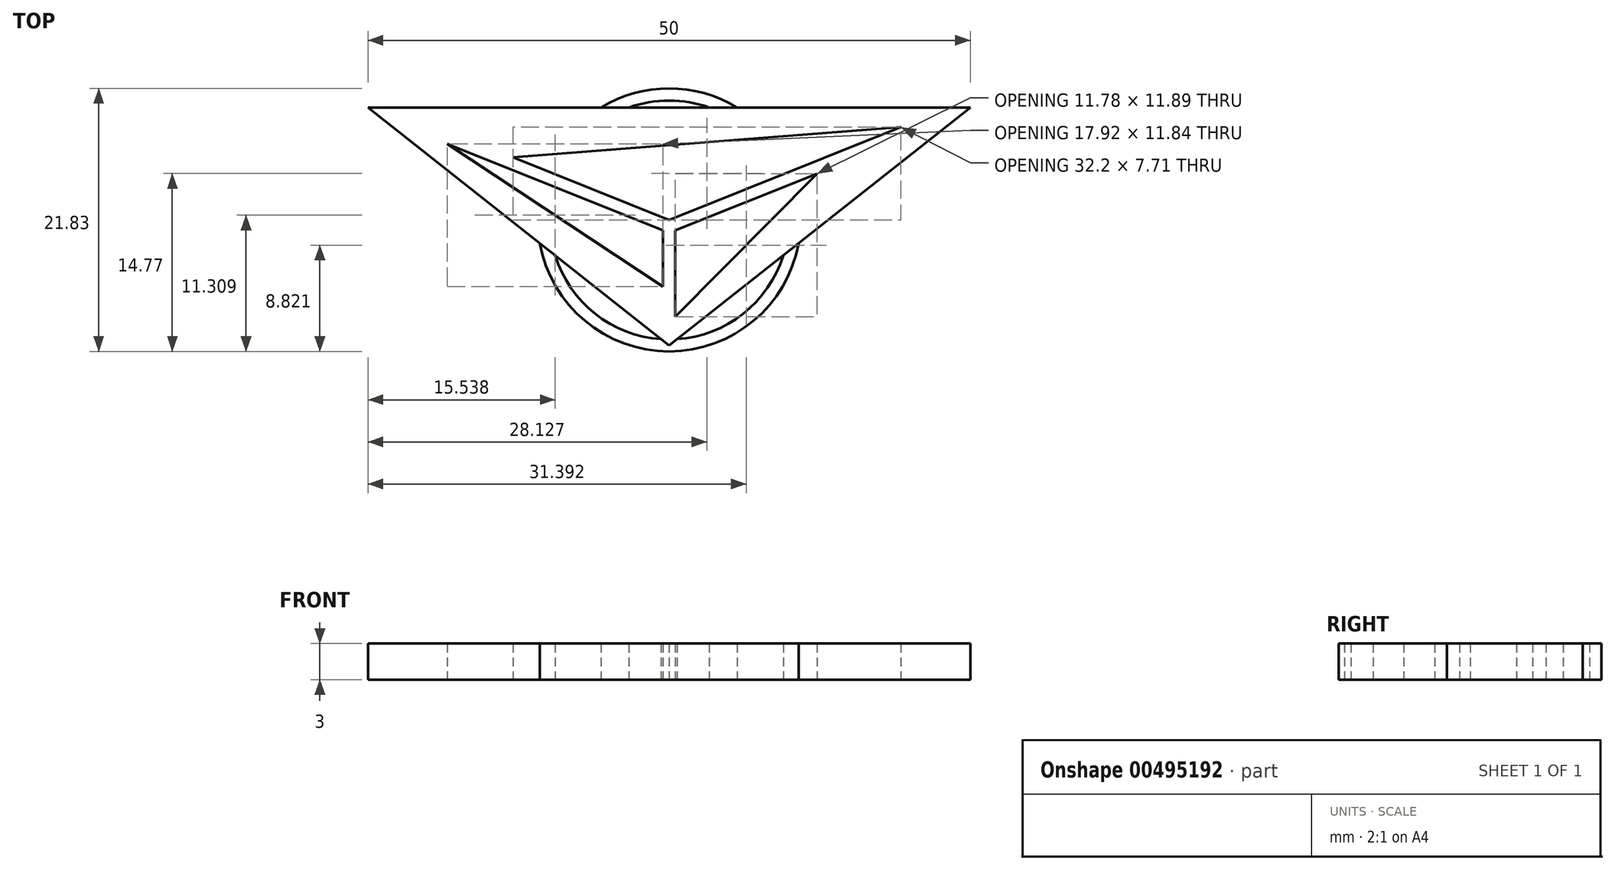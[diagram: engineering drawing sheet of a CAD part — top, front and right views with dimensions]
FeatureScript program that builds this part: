
annotation { "Feature Type Name" : "Feature", "Feature Type Description" : "" }
export const myFeature = defineFeature(function(context is Context, id is Id, definition is map)
    precondition{}
    {
        {
            var Q0;
            Q0=qCreatedBy(makeId("Top.planeOp"),FACE);
            var sketch = newSketch(context, id + "F0", { "sketchPlane" : qUnion([Q0])});
            skLineSegment(sketch, "E0", {"start": v(0, 0) * mm, "end": v(25, 0) * mm});
            skLineSegment(sketch, "E1", {"start": v(25, 0) * mm, "end": v(0, -19.75) * mm});
            skLineSegment(sketch, "E2", {"start": v(0, -19.75) * mm, "end": v(-25, 0) * mm});
            skLineSegment(sketch, "E3", {"start": v(-25, 0) * mm, "end": v(0, 0) * mm});
            skLineSegment(sketch, "E4.0", {"start": v(-22.12, -1) * mm, "end": v(0, -1) * mm});
            skPoint(sketch, "E5", {"position": v(0, -9.88) * mm});
            skLineSegment(sketch, "E6", {"start": v(0, -1) * mm, "end": v(22.12, -1) * mm});
            skLineSegment(sketch, "E7.0", {"start": v(22.12, -1) * mm, "end": v(0, -18.48) * mm});
            skLineSegment(sketch, "E8.0", {"start": v(0, -18.48) * mm, "end": v(-22.12, -1) * mm});
            skLineSegment(sketch, "E9", {"start": v(0, 0) * mm, "end": v(0, -19.75) * mm, "construction": true});
            skLineSegment(sketch, "E10", {"start": v(-22.12, -1) * mm, "end": v(0, -9.88) * mm, "construction": true});
            skLineSegment(sketch, "E11.0", {"start": v(-20.74, -2.1) * mm, "end": v(-0.5, -10.21) * mm});
            skLineSegment(sketch, "E12.0", {"start": v(-20.78, -1) * mm, "end": v(0, -9.34) * mm});
            skLineSegment(sketch, "E13.0", {"start": v(-0.5, -2.16) * mm, "end": v(-0.5, -18.08) * mm});
            skLineSegment(sketch, "E14.0", {"start": v(0.5, -2.08) * mm, "end": v(0.5, -18.08) * mm});
            skLineSegment(sketch, "E15", {"start": v(22.12, -1) * mm, "end": v(0, -9.88) * mm, "construction": true});
            skLineSegment(sketch, "E16.0", {"start": v(20.78, -1) * mm, "end": v(0, -9.34) * mm});
            skLineSegment(sketch, "E17.0", {"start": v(20.74, -2.1) * mm, "end": v(0.5, -10.21) * mm});
            skPoint(sketch, "E18", {"position": v(-14.02, -3.71) * mm});
            skPoint(sketch, "E19", {"position": v(13.45, -5.02) * mm});
            skPoint(sketch, "E20", {"position": v(-0.5, -15.46) * mm});
            skLineSegment(sketch, "E21", {"start": v(-14.02, -3.71) * mm, "end": v(20.78, -1) * mm, "construction": true});
            skLineSegment(sketch, "E22", {"start": v(13.45, -5.02) * mm, "end": v(0.5, -18.08) * mm, "construction": true});
            skLineSegment(sketch, "E23", {"start": v(-0.5, -15.46) * mm, "end": v(-20.74, -2.1) * mm, "construction": true});
            skLineSegment(sketch, "E24.0", {"start": v(-12.97, -4.13) * mm, "end": v(19.23, -1.62) * mm});
            skLineSegment(sketch, "E25.0", {"start": v(-15.07, -3.3) * mm, "end": v(14.34, -1) * mm});
            skLineSegment(sketch, "E26.0", {"start": v(12.28, -5.49) * mm, "end": v(0.5, -17.37) * mm});
            skLineSegment(sketch, "E27.0", {"start": v(14.62, -4.55) * mm, "end": v(3.75, -15.52) * mm});
            skLineSegment(sketch, "E28.0", {"start": v(-0.5, -14.86) * mm, "end": v(-18.42, -3.02) * mm});
            skLineSegment(sketch, "E29.0", {"start": v(-0.5, -16.06) * mm, "end": v(-16.11, -5.75) * mm});
            skPoint(sketch, "E30.positionSnap0", {"position": v(10.62, -6.15) * mm});
            skPoint(sketch, "E31", {"position": v(11.06, -5.44) * mm});
            skPoint(sketch, "E32", {"position": v(-9.47, -12.27) * mm});
            skPoint(sketch, "E33", {"position": v(-10.74, -11.26) * mm});
            skPoint(sketch, "E34", {"position": v(9.47, -12.27) * mm});
            skPoint(sketch, "E35", {"position": v(10.74, -11.26) * mm});
            skPoint(sketch, "E36", {"position": v(5.65, 0) * mm});
            skPoint(sketch, "E37", {"position": v(3.33, 0) * mm});
            skPoint(sketch, "E38", {"position": v(-3.33, 0) * mm});
            skPoint(sketch, "E39", {"position": v(-5.65, 0) * mm});
            skCircle(sketch, "E40", {"center": v(0, -9.34) * mm, "radius": 10.41 * mm, "construction": true});
            skArc(sketch, "E41", {"start": v(-10.74, -11.26) * mm, "mid": v(0, -20.25) * mm, "end": v(10.74, -11.26) * mm});
            skArc(sketch, "E42", {"start": v(-9.47, -12.27) * mm, "mid": v(-6.15, -17.12) * mm, "end": v(-0.66, -19.23) * mm});
            skArc(sketch, "E43", {"start": v(5.65, 0) * mm, "mid": v(0, 1.58) * mm, "end": v(-5.65, 0) * mm});
            skArc(sketch, "E44", {"start": v(3.33, 0) * mm, "mid": v(0, 0.58) * mm, "end": v(-3.33, 0) * mm});
            skArc(sketch, "E45.trimOffspring", {"start": v(0.66, -19.23) * mm, "mid": v(6.15, -17.12) * mm, "end": v(9.47, -12.27) * mm});
            skSolve(sketch);
        }
        {
            var Q0;
            Q0=makeQuery(id+"F0.imprint","IMPRINT",FACE,{"disambiguationData":[TD([[makeQuery(id+"F0.imprint","IMPRINT",EDGE,{"derivedFrom":sQuery(id+"F0.wireOp",EDGE,"E0")}),-1.0]])]});
            var Q1;
            {var subQ0=sQuery(id+"F0.wireOp",EDGE,"E26.0");Q1=makeQuery(id+"F0.imprint","IMPRINT",FACE,{"disambiguationData":[TD([[makeQuery(id+"F0.imprint","IMPRINT",EDGE,{"derivedFrom":subQ0}),1.0]])]});}
            var Q2;
            {var subQ7=sQuery(id+"F0.wireOp",EDGE,"E8.0");var subQ12=sQuery(id+"F0.wireOp",EDGE,"E7.0");var subQ13=makeQuery(id+"F0.imprint","INTERSECT",VERTEX,{"derivedFrom":[subQ12,subQ7]});Q2=makeQuery(id+"F0.imprint","IMPRINT",FACE,{"disambiguationData":[TD([[makeQuery(id+"F0.imprint","IMPRINT",EDGE,{"disambiguationData":[TD([[subQ13,1.0]])],"derivedFrom":subQ12}),-1.0]])]});}
            var Q3;
            {var subQ5=sQuery(id+"F0.wireOp",EDGE,"E7.0");var subQ6=sQuery(id+"F0.wireOp",EDGE,"E6");var subQ7=makeQuery(id+"F0.imprint","INTERSECT",VERTEX,{"derivedFrom":[subQ6,subQ5]});Q3=makeQuery(id+"F0.imprint","IMPRINT",FACE,{"disambiguationData":[TD([[makeQuery(id+"F0.imprint","IMPRINT",EDGE,{"disambiguationData":[TD([[subQ7,1.0]])],"derivedFrom":subQ6}),-1.0]])]});}
            var Q4;
            {var subQ1=sQuery(id+"F0.wireOp",EDGE,"E16.0");var subQ5=sQuery(id+"F0.wireOp",EDGE,"E6");var subQ6=makeQuery(id+"F0.imprint","INTERSECT",VERTEX,{"derivedFrom":[subQ5,subQ1]});Q4=makeQuery(id+"F0.imprint","IMPRINT",FACE,{"disambiguationData":[TD([[makeQuery(id+"F0.imprint","IMPRINT",EDGE,{"disambiguationData":[TD([[subQ6,1.0]])],"derivedFrom":subQ5}),-1.0]])]});}
            var Q5;
            {var subQ0=sQuery(id+"F0.wireOp",EDGE,"E25.0");var subQ1=sQuery(id+"F0.wireOp",EDGE,"E13.0");var subQ2=makeQuery(id+"F0.imprint","INTERSECT",VERTEX,{"derivedFrom":[subQ1,subQ0]});Q5=makeQuery(id+"F0.imprint","IMPRINT",FACE,{"disambiguationData":[TD([[makeQuery(id+"F0.imprint","IMPRINT",EDGE,{"disambiguationData":[TD([[subQ2,-1.0]])],"derivedFrom":subQ1}),1.0]])]});}
            var Q6;
            {var subQ0=sQuery(id+"F0.wireOp",EDGE,"E24.0");var subQ1=sQuery(id+"F0.wireOp",EDGE,"E12.0");var subQ2=makeQuery(id+"F0.imprint","INTERSECT",VERTEX,{"derivedFrom":[subQ1,subQ0]});Q6=makeQuery(id+"F0.imprint","IMPRINT",FACE,{"disambiguationData":[TD([[makeQuery(id+"F0.imprint","IMPRINT",EDGE,{"disambiguationData":[TD([[subQ2,1.0]])],"derivedFrom":subQ1}),1.0]])]});}
            var Q7;
            {var subQ4=sQuery(id+"F0.wireOp",EDGE,"E8.0");var subQ6=sQuery(id+"F0.wireOp",EDGE,"E4.0");var subQ7=makeQuery(id+"F0.imprint","INTERSECT",VERTEX,{"derivedFrom":[subQ6,subQ4]});Q7=makeQuery(id+"F0.imprint","IMPRINT",FACE,{"disambiguationData":[TD([[makeQuery(id+"F0.imprint","IMPRINT",EDGE,{"disambiguationData":[TD([[subQ7,-1.0]])],"derivedFrom":subQ6}),-1.0]])]});}
            var Q8;
            {var subQ0=sQuery(id+"F0.wireOp",EDGE,"E28.0");Q8=makeQuery(id+"F0.imprint","IMPRINT",FACE,{"disambiguationData":[TD([[makeQuery(id+"F0.imprint","IMPRINT",EDGE,{"derivedFrom":subQ0}),1.0]])]});}
            var Q9;
            {var subQ0=sQuery(id+"F0.wireOp",EDGE,"Rau6Xa31-grvz-TC1c-qM9h-ZFH14MHzaVjz");Q9=makeQuery(id+"F0.imprint","IMPRINT",FACE,{"disambiguationData":[TD([[makeQuery(id+"F0.imprint","IMPRINT",EDGE,{"derivedFrom":subQ0}),1.0]])]});}
            var Q10;
            {var subQ0=sQuery(id+"F0.wireOp",EDGE,"0mO2l9Ov-tcdl-7pQF-Do68-VygC9JScL4KG");Q10=makeQuery(id+"F0.imprint","IMPRINT",FACE,{"disambiguationData":[TD([[makeQuery(id+"F0.imprint","IMPRINT",EDGE,{"derivedFrom":subQ0}),1.0]])]});}
            extrude(context, id + "F1", {"entities" : qUnion([Q0, Q1, Q2, Q3, Q4, Q5, Q6, Q7, Q8, Q9, Q10]), "depth" : 3 * mm});
        }
        {
            var Q0;
            {var subQ1=sQuery(id+"F0.wireOp",EDGE,"E4.0");var subQ6=sQuery(id+"F0.wireOp",EDGE,"E6");var subQ7=makeQuery(id+"F0.imprint","INTERSECT",VERTEX,{"derivedFrom":[subQ1,subQ6]});Q0=makeQuery(id+"F0.imprint","IMPRINT",FACE,{"disambiguationData":[TD([[makeQuery(id+"F0.imprint","IMPRINT",EDGE,{"disambiguationData":[TD([[subQ7,1.0]])],"derivedFrom":subQ1}),-1.0]])]});}
            var Q1;
            {var subQ3=sQuery(id+"F0.wireOp",EDGE,"E27.0");Q1=makeQuery(id+"F0.imprint","IMPRINT",FACE,{"disambiguationData":[TD([[makeQuery(id+"F0.imprint","IMPRINT",EDGE,{"derivedFrom":subQ3}),1.0]])]});}
            var Q2;
            {var subQ3=sQuery(id+"F0.wireOp",EDGE,"E29.0");Q2=makeQuery(id+"F0.imprint","IMPRINT",FACE,{"disambiguationData":[TD([[makeQuery(id+"F0.imprint","IMPRINT",EDGE,{"derivedFrom":subQ3}),1.0]])]});}
            extrude(context, id + "F2", {"entities" : qUnion([Q0, Q1, Q2]), "operationType" : NewBodyOperationType.ADD, "depth" : 3 * mm});
        }
        {
            var Q0;
            {var subQ0=sQuery(id+"F0.wireOp",EDGE,"E43");Q0=makeQuery(id+"F0.imprint","IMPRINT",FACE,{"disambiguationData":[TD([[makeQuery(id+"F0.imprint","IMPRINT",EDGE,{"derivedFrom":subQ0}),1.0]])]});}
            var Q1;
            {var subQ5=sQuery(id+"F0.wireOp",EDGE,"E41");Q1=makeQuery(id+"F0.imprint","IMPRINT",FACE,{"disambiguationData":[TD([[makeQuery(id+"F0.imprint","IMPRINT",EDGE,{"derivedFrom":subQ5}),1.0]])]});}
            extrude(context, id + "F3", {"entities" : qUnion([Q0, Q1]), "depth" : 3 * mm});
        }
    });
